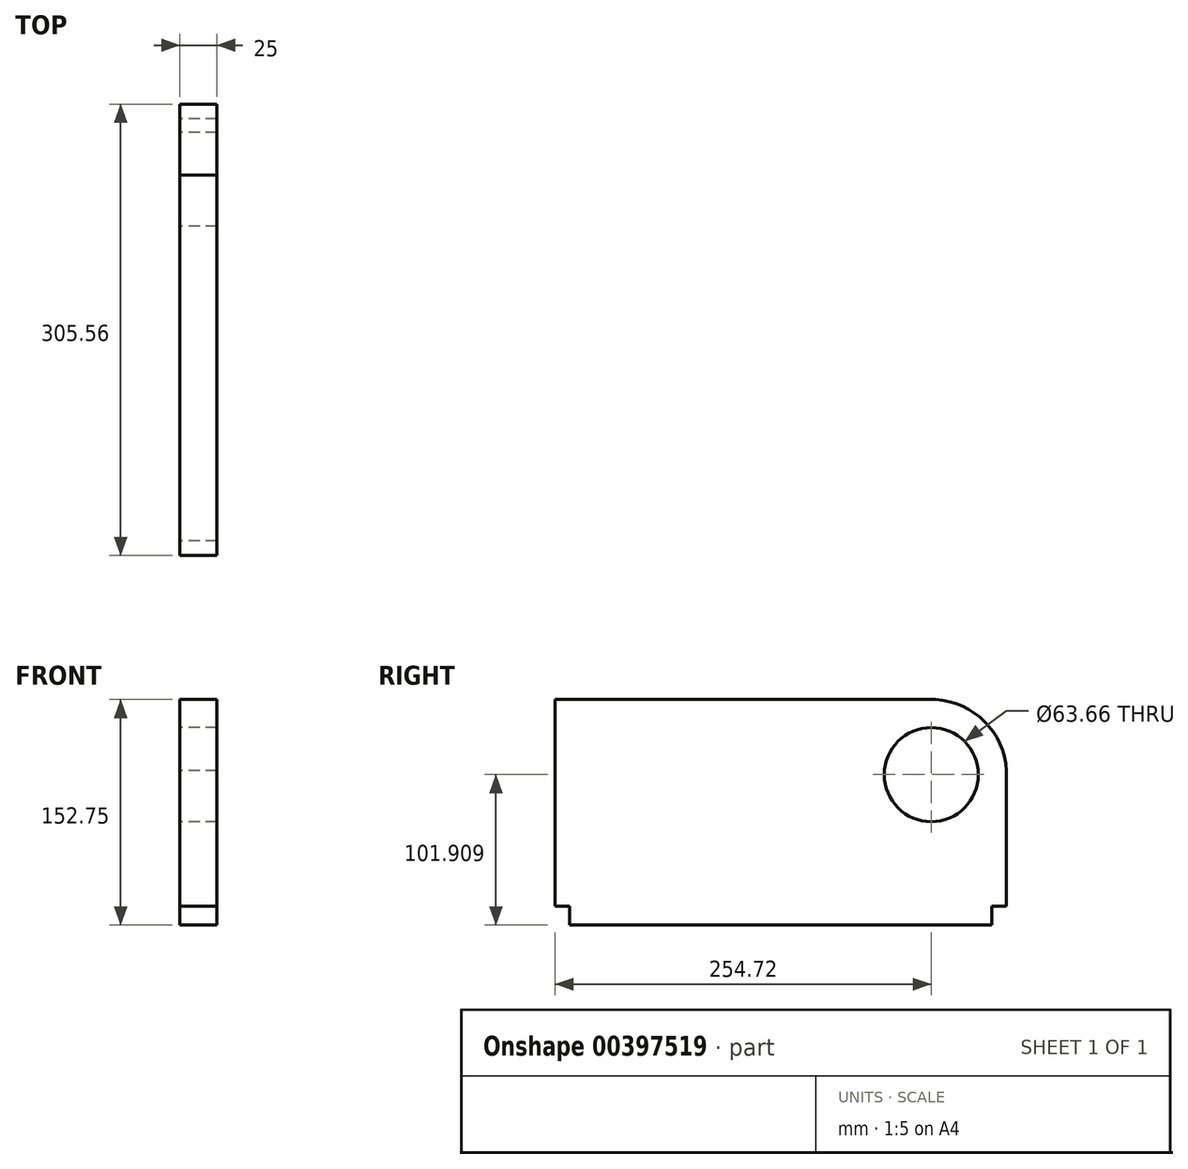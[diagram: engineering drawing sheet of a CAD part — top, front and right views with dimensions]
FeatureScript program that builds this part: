
annotation { "Feature Type Name" : "Feature", "Feature Type Description" : "" }
export const myFeature = defineFeature(function(context is Context, id is Id, definition is map)
    precondition{}
    {
        {
            var Q0;
            Q0=qCreatedBy(makeId("Right.planeOp"),FACE);
            var sketch = newSketch(context, id + "F0", { "sketchPlane" : qUnion([Q0])});
            skCircle(sketch, "E0", {"center": v(-72.14, 429.08) * mm, "radius": 15.87 * mm});
            skCircle(sketch, "E1", {"center": v(-72.14, 429.08) * mm, "radius": 31.83 * mm});
            skLineSegment(sketch, "E2", {"start": v(-31.2, 339.87) * mm, "end": v(-316.95, 339.87) * mm});
            skLineSegment(sketch, "E3", {"start": v(-316.95, 339.87) * mm, "end": v(-316.95, 327.17) * mm});
            skLineSegment(sketch, "E4", {"start": v(-316.95, 327.17) * mm, "end": v(-31.2, 327.17) * mm});
            skLineSegment(sketch, "E5", {"start": v(-31.2, 327.17) * mm, "end": v(-31.2, 339.87) * mm});
            skLineSegment(sketch, "E6", {"start": v(-326.86, 479.92) * mm, "end": v(-326.86, 339.87) * mm});
            skLineSegment(sketch, "E7", {"start": v(-326.86, 339.87) * mm, "end": v(-21.3, 339.87) * mm});
            skLineSegment(sketch, "E8", {"start": v(-21.3, 339.87) * mm, "end": v(-21.3, 431.78) * mm});
            skArc(sketch, "E9", {"start": v(-21.3, 431.78) * mm, "mid": v(-36.14, 465.08) * mm, "end": v(-69.44, 479.92) * mm});
            skLineSegment(sketch, "E10", {"start": v(-69.44, 479.92) * mm, "end": v(-326.86, 479.92) * mm});
            skSolve(sketch);
        }
        {
            var Q0;
            Q0 = qSketchRegion(id + "F0", true);
            extrude(context, id + "F1", {"entities" : qUnion([Q0]), "depth" : 25 * mm});
        }
    });
